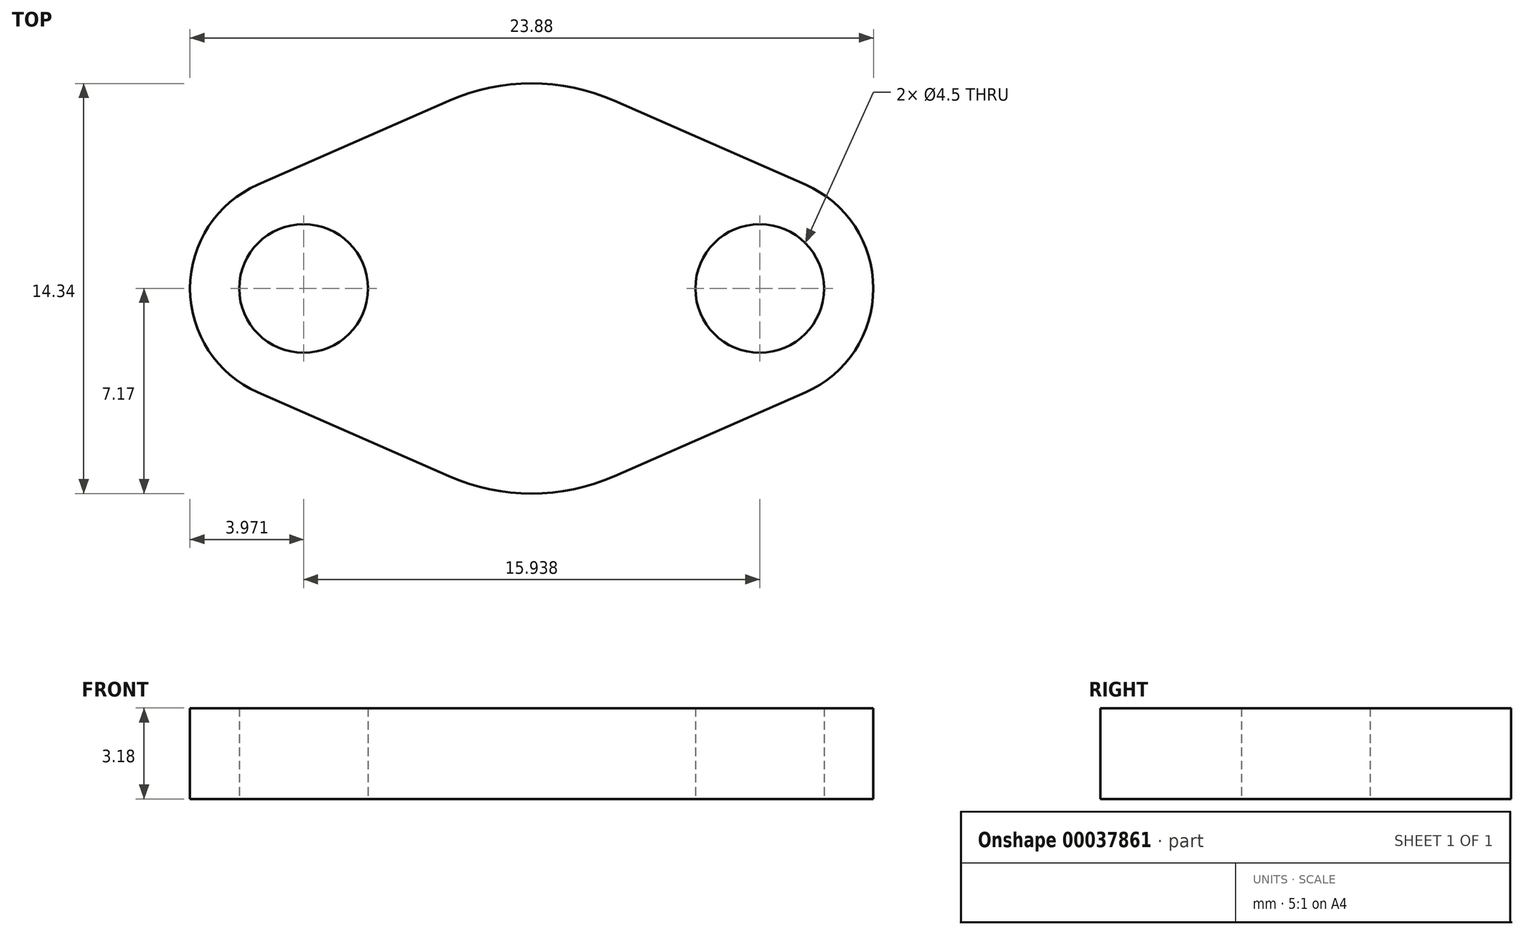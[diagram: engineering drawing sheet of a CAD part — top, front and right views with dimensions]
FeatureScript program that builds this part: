
annotation { "Feature Type Name" : "Feature", "Feature Type Description" : "" }
export const myFeature = defineFeature(function(context is Context, id is Id, definition is map)
    precondition{}
    {
        {
            var Q0;
            Q0=qCreatedBy(makeId("Top.planeOp"),FACE);
            var sketch = newSketch(context, id + "F0", { "sketchPlane" : qUnion([Q0])});
            skArc(sketch, "E0", {"start": v(-9.57, 3.63) * mm, "mid": v(-11.94, 0) * mm, "end": v(-9.57, -3.63) * mm});
            skLineSegment(sketch, "E1", {"start": v(-9.57, 3.63) * mm, "end": v(-2.89, 6.57) * mm});
            skLineSegment(sketch, "E2", {"start": v(-2.89, -6.57) * mm, "end": v(-9.57, -3.63) * mm});
            skArc(sketch, "E3", {"start": v(-2.89, -6.57) * mm, "mid": v(0, -7.17) * mm, "end": v(2.89, -6.57) * mm});
            skLineSegment(sketch, "E4", {"start": v(9.57, -3.63) * mm, "end": v(2.89, -6.57) * mm});
            skLineSegment(sketch, "E5", {"start": v(2.89, 6.57) * mm, "end": v(9.57, 3.63) * mm});
            skLineSegment(sketch, "E6", {"start": v(7.97, 0) * mm, "end": v(-7.97, 0) * mm, "construction": true});
            skArc(sketch, "E7", {"start": v(9.57, -3.63) * mm, "mid": v(11.94, 0) * mm, "end": v(9.57, 3.63) * mm});
            skArc(sketch, "E8", {"start": v(2.89, 6.57) * mm, "mid": v(0, 7.17) * mm, "end": v(-2.89, 6.57) * mm});
            skCircle(sketch, "E9", {"center": v(-7.97, 0) * mm, "radius": 2.25 * mm});
            skCircle(sketch, "E10", {"center": v(7.97, 0) * mm, "radius": 2.25 * mm});
            skSolve(sketch);
        }
        {
            var Q0;
            Q0 = qSketchRegion(id + "F0", true);
            extrude(context, id + "F1", {"entities" : qUnion([Q0]), "depth" : 3.17 * mm});
        }
    });
